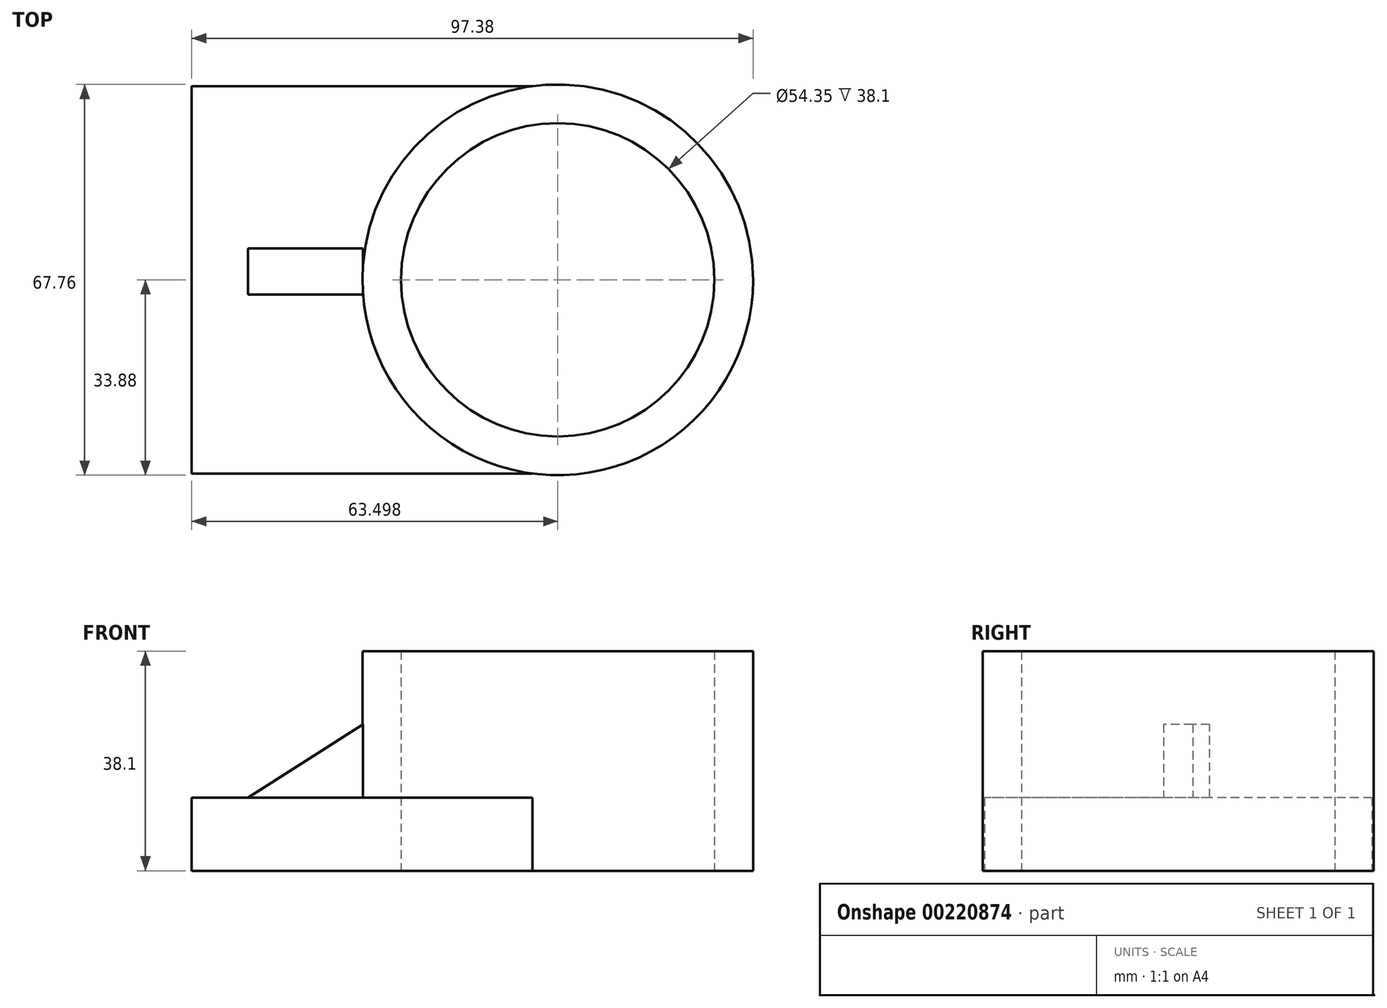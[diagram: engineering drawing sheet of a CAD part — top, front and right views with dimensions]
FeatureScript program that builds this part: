
annotation { "Feature Type Name" : "Feature", "Feature Type Description" : "" }
export const myFeature = defineFeature(function(context is Context, id is Id, definition is map)
    precondition{}
    {
        {
            var Q0;
            Q0=qCreatedBy(makeId("Top.planeOp"),FACE);
            var sketch = newSketch(context, id + "F0", { "sketchPlane" : qUnion([Q0])});
            skLineSegment(sketch, "E0.bottom", {"start": v(-48.72, 36.14) * mm, "end": v(14.78, 36.14) * mm});
            skLineSegment(sketch, "E0.top", {"start": v(-48.72, -31.06) * mm, "end": v(14.78, -31.06) * mm});
            skLineSegment(sketch, "E0.left", {"start": v(-48.72, 36.14) * mm, "end": v(-48.72, -31.06) * mm});
            skLineSegment(sketch, "E0.right", {"start": v(14.78, 36.14) * mm, "end": v(14.78, -31.06) * mm});
            skCircle(sketch, "E1", {"center": v(14.78, 2.54) * mm, "radius": 33.88 * mm});
            skCircle(sketch, "E2", {"center": v(14.78, 2.54) * mm, "radius": 27.17 * mm});
            skSolve(sketch);
        }
        {
            var Q0;
            {var subQ0=sQuery(id+"F0.wireOp",EDGE,"E0.left");Q0=makeQuery(id+"F0.imprint","IMPRINT",FACE,{"disambiguationData":[TD([[makeQuery(id+"F0.imprint","IMPRINT",EDGE,{"derivedFrom":subQ0}),1.0]])]});}
            extrude(context, id + "F1", {"entities" : qUnion([Q0]), "depth" : 12.7 * mm});
        }
        {
            var Q0;
            {var subQ0=sQuery(id+"F0.wireOp",EDGE,"E0.right");var subQ5=sQuery(id+"F0.wireOp",EDGE,"E0.bottom");var subQ6=makeQuery(id+"F0.imprint","INTERSECT",VERTEX,{"derivedFrom":[subQ5,subQ0]});Q0=makeQuery(id+"F0.imprint","IMPRINT",FACE,{"disambiguationData":[TD([[makeQuery(id+"F0.imprint","IMPRINT",EDGE,{"disambiguationData":[TD([[subQ6,1.0]])],"derivedFrom":subQ5}),1.0]])]});}
            var Q1;
            {var subQ0=sQuery(id+"F0.wireOp",EDGE,"E0.right");var subQ5=sQuery(id+"F0.wireOp",EDGE,"E0.bottom");var subQ6=makeQuery(id+"F0.imprint","INTERSECT",VERTEX,{"derivedFrom":[subQ5,subQ0]});Q1=makeQuery(id+"F0.imprint","IMPRINT",FACE,{"disambiguationData":[TD([[makeQuery(id+"F0.imprint","IMPRINT",EDGE,{"disambiguationData":[TD([[subQ6,1.0]])],"derivedFrom":subQ5}),-1.0]])]});}
            extrude(context, id + "F2", {"entities" : qUnion([Q0, Q1]), "operationType" : NewBodyOperationType.ADD, "depth" : 38.1 * mm});
        }
        {
            var Q0;
            Q0=makeQuery(id+"F1.opExtrude","CAP_FACE",FACE,{"disambiguationData":[OSD([sQuery(id+"F0.wireOp",EDGE,"E0.bottom"),sQuery(id+"F0.wireOp",EDGE,"E0.top"),sQuery(id+"F0.wireOp",EDGE,"E0.left"),sQuery(id+"F0.wireOp",EDGE,"E1")])],"isStart":false});
            var sketch = newSketch(context, id + "F3", { "sketchPlane" : qUnion([Q0])});
            skLineSegment(sketch, "E3.bottom", {"start": v(-38.95, 8) * mm, "end": v(-19, 8) * mm});
            skLineSegment(sketch, "E3.top", {"start": v(-38.95, 0) * mm, "end": v(-19, 0) * mm});
            skLineSegment(sketch, "E3.left", {"start": v(-38.95, 8) * mm, "end": v(-38.95, 0) * mm});
            skLineSegment(sketch, "E3.right", {"start": v(-19, 8) * mm, "end": v(-19, 0) * mm});
            skSolve(sketch);
        }
        {
            var Q0;
            Q0 = qSketchRegion(id + "F3", true);
            extrude(context, id + "F4", {"entities" : qUnion([Q0]), "operationType" : NewBodyOperationType.ADD, "depth" : 12.7 * mm});
        }
        {
            var Q0;
            Q0=makeQuery(id+"F4.opExtrude","SWEPT_FACE",FACE,{"disambiguationData":[OSD([sQuery(id+"F3.wireOp",EDGE,"E3.top")])]});
            var sketch = newSketch(context, id + "F5", { "sketchPlane" : qUnion([Q0])});
            skLineSegment(sketch, "E4", {"start": v(-19, 25.4) * mm, "end": v(-38.95, 12.7) * mm});
            skSolve(sketch);
        }
        {
            var Q0;
            Q0=makeQuery(id+"F5.imprint","IMPRINT",FACE,{"disambiguationData":[TD([[makeQuery(id+"F5.imprint","IMPRINT",EDGE,{"derivedFrom":sQuery(id+"F5.wireOp",EDGE,"E4")}),-1.0]])]});
            extrude(context, id + "F6", {"entities" : qUnion([Q0]), "operationType" : NewBodyOperationType.REMOVE, "oppositeDirection" : true, "depth" : 25.4 * mm});
        }
    });
